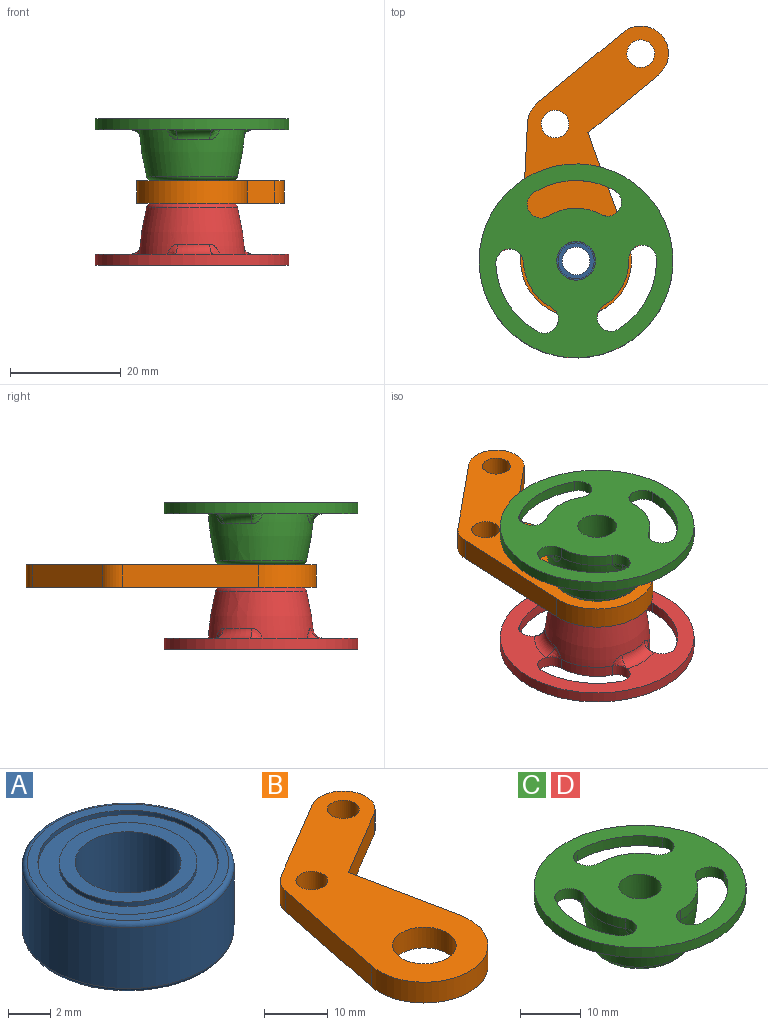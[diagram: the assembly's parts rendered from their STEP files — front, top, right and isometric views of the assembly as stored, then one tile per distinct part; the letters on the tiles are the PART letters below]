
ASSEMBLY  parts=4 mates=7
PART A: 14 faces, bbox 10.8x10.8x4 mm
  f0: plane 6.5x6.5mm, normal (0,0,-1), area 13.5mm2, adj f2,f9
  f1: plane 6.5x6.5mm, normal (0,0,1), area 13.5mm2, adj f2,f6
  f2: cylinder r=2.5mm len=5mm, axis (0,0,-1), area 62.8mm2, adj f0,f1
  f3: cylinder r=5mm len=10mm, axis (0,0,-1), area 110mm2, adj f12,f13
  f4: plane 9.5x9.5mm, normal (0,0,1), area 14.1mm2, adj f7,f13
  f5: plane 9.5x9.5mm, normal (0,0,-1), area 14.1mm2, adj f10,f12
  f6: cylinder r=3.25mm len=6.5mm, axis (0,0,1), area 5.1mm2, adj f1,f8
  f7: cylinder r=4.25mm len=8.5mm, axis (0,0,1), area 6.7mm2, adj f4,f8
  f8: plane 8.5x8.5mm, normal (0,0,1), area 23.6mm2, adj f6,f7
  f9: cylinder r=3.25mm len=6.5mm, axis (0,0,-1), area 5.1mm2, adj f0,f11
  f10: cylinder r=4.25mm len=8.5mm, axis (0,0,-1), area 6.7mm2, adj f5,f11
  f11: plane 8.5x8.5mm, normal (0,0,-1), area 23.6mm2, adj f9,f10
  f12: torus R=4.75mm, axis (0,0,1), area 12.1mm2, adj f3,f5
  f13: torus R=4.75mm, axis (0,0,1), area 12.1mm2, adj f3,f4
PART B: 12 faces, bbox 32.2x50.2x4 mm
  f0: plane 17.2x10.21mm, normal (-0.51,0.86,0), area 80mm2, adj f1,f8,f10,f11
  f1: cylinder r=5mm len=4mm, axis (0,0,-1), area 16.7mm2, adj f0,f2,f10,f11
  f2: plane 24x4.9mm, normal (-0.98,0.2,0), area 98mm2, adj f1,f3,f10,f11
  f3: cylinder r=10mm len=20mm, axis (0,0,-1), area 141.8mm2, adj f2,f4,f10,f11
  f4: plane 20.52x4.19mm, normal (0.98,0.2,0), area 83.8mm2, adj f3,f5,f10,f11
  f5: plane 14.14x8.4mm, normal (0.51,-0.86,0), area 65.8mm2, adj f4,f8,f10,f11
  f6: cylinder r=5mm len=10mm, axis (0,0,-1), area 125.7mm2, adj f10,f11
  f7: cylinder r=2.5mm len=5mm, axis (0,0,-1), area 62.8mm2, adj f10,f11
  f8: cylinder r=5mm len=9.3mm, axis (0,0,-1), area 62.8mm2, adj f0,f5,f10,f11
  f9: cylinder r=2.5mm len=5mm, axis (0,0,-1), area 62.8mm2, adj f10,f11
  f10: plane 50.21x32.2mm, normal (0,0,1), area 658.7mm2, adj f0,f1,f2,f3,f4,f5,f6,f7
  f11: plane 50.21x32.2mm, normal (0,0,-1), area 658.7mm2, adj f0,f1,f2,f3,f4,f5,f6,f7
PART C: 30 faces, bbox 35x35x11.3 mm
  f0: cylinder r=3.5mm len=7.25mm, axis (0,0,1), area 159.4mm2, adj f1,f28
  f1: plane 35x35mm, normal (0,0,1), area 676.2mm2, adj f0,f3,f4,f5,f6,f7,f8,f9
  f2: plane 35x35mm, normal (0,0,-1), area 389.1mm2, adj f3,f4,f6,f7,f9,f10,f11,f12
  f3: cylinder r=17.5mm len=35mm, axis (0,0,-1), area 219.9mm2, adj f1,f2
  f4: cylinder r=2.5mm len=5mm, axis (0,0,-1), area 15.7mm2, adj f1,f2,f5,f7,f21
  f5: cylinder r=9.5mm len=8.23mm, axis (0,0,-1), area 19.9mm2, adj f1,f4,f6,f16
  f6: cylinder r=2.5mm len=4.67mm, axis (0,0,-1), area 15.7mm2, adj f1,f2,f5,f7,f26
  f7: cylinder r=14.5mm len=12.56mm, axis (0,0,-1), area 30.4mm2, adj f1,f2,f4,f6
  f8: cylinder r=9.5mm len=9.5mm, axis (0,0,-1), area 19.9mm2, adj f1,f9,f11,f16
  f9: cylinder r=2.5mm len=4.67mm, axis (0,0,-1), area 15.7mm2, adj f1,f2,f8,f10,f23
  f10: cylinder r=14.5mm len=14.5mm, axis (0,0,-1), area 30.4mm2, adj f1,f2,f9,f11
  f11: cylinder r=2.5mm len=4.67mm, axis (0,0,-1), area 15.7mm2, adj f1,f2,f8,f10,f18
  f12: cylinder r=2.5mm len=5mm, axis (0,0,-1), area 15.7mm2, adj f1,f2,f13,f15,f20
  f13: cylinder r=14.5mm len=12.56mm, axis (0,0,-1), area 30.4mm2, adj f1,f2,f12,f14
  f14: cylinder r=2.5mm len=4.67mm, axis (0,0,-1), area 15.7mm2, adj f1,f2,f13,f15,f24
  f15: cylinder r=9.5mm len=8.23mm, axis (0,0,-1), area 19.9mm2, adj f1,f12,f14,f16
  f16: revolved ~19x19mm, area 438.4mm2, adj f5,f8,f15,f18,f19,f20,f21,f22
  f17: plane 14.46x14.46mm, normal (0,0,-1), area 85.6mm2, adj f27,f29
  f18: bspline ~2.86x1.85mm, area 3.1mm2, adj f11,f16,f19
  f19: torus R=11.35mm, axis (0,0,1), area 18.9mm2, adj f2,f16,f18,f20
  f20: bspline ~2.35x2.05mm, area 3.1mm2, adj f12,f16,f19
  f21: bspline ~2.35x2.05mm, area 3.1mm2, adj f4,f16,f22
  f22: torus R=11.35mm, axis (0,0,1), area 18.9mm2, adj f2,f16,f21,f23
  f23: bspline ~2.86x1.85mm, area 3.1mm2, adj f9,f16,f22
  f24: bspline ~2.61x2.12mm, area 3.1mm2, adj f14,f16,f25
  f25: torus R=11.35mm, axis (0,0,1), area 18.9mm2, adj f2,f16,f24,f26
  f26: bspline ~2.61x2.12mm, area 3.1mm2, adj f6,f16,f25
  f27: torus R=7.23mm, axis (0,0,1), area 64.8mm2, adj f16,f17
  f28: plane 10x10mm, normal (0,0,-1), area 40.1mm2, adj f0,f29
  f29: cylinder r=5mm len=10mm, axis (0,0,-1), area 125.7mm2, adj f17,f28
PART D: same geometry as C
PLACE A rot(axis=(1,0,0),180deg) t=(0.48,-7.1,-25.16)mm fixed
PLACE B rot(axis=(0,0,1),8.7deg) t=(0.48,-7.1,-29.16)mm
PLACE C rot(axis=(0,0,1),151.7deg) t=(0.48,-7.1,-15.91)mm
PLACE D rot(axis=(-0.24,-0.97,0),180deg) t=(0.48,-7.1,-38.41)mm
MATE cylindrical D.f0 <-> A.f2  axis (0,0,-1) through (0.48,-7.1,-36.78)mm
MATE planar A.f7 <-> D.f5  axis (0,0,-1) through (0.48,-7.1,-29.16)mm
MATE cylindrical C.f0 <-> A.f2  axis (0,0,1) through (0.48,-7.1,-17.53)mm
MATE cylindrical C.f12 <-> D.f4  axis (0,0,-1) through (-5.21,-17.66,-13.91)mm
MATE cylindrical B.f6 <-> A.f3  axis (0,0,-1) through (0.48,-7.1,-27.16)mm
MATE planar B.f3 <-> A.f3  axis (0,0,-1) through (0.48,-7.1,-27.16)mm
MATE planar A.f10 <-> C.f5  axis (0,0,1) through (0.48,-7.1,-25.16)mm
